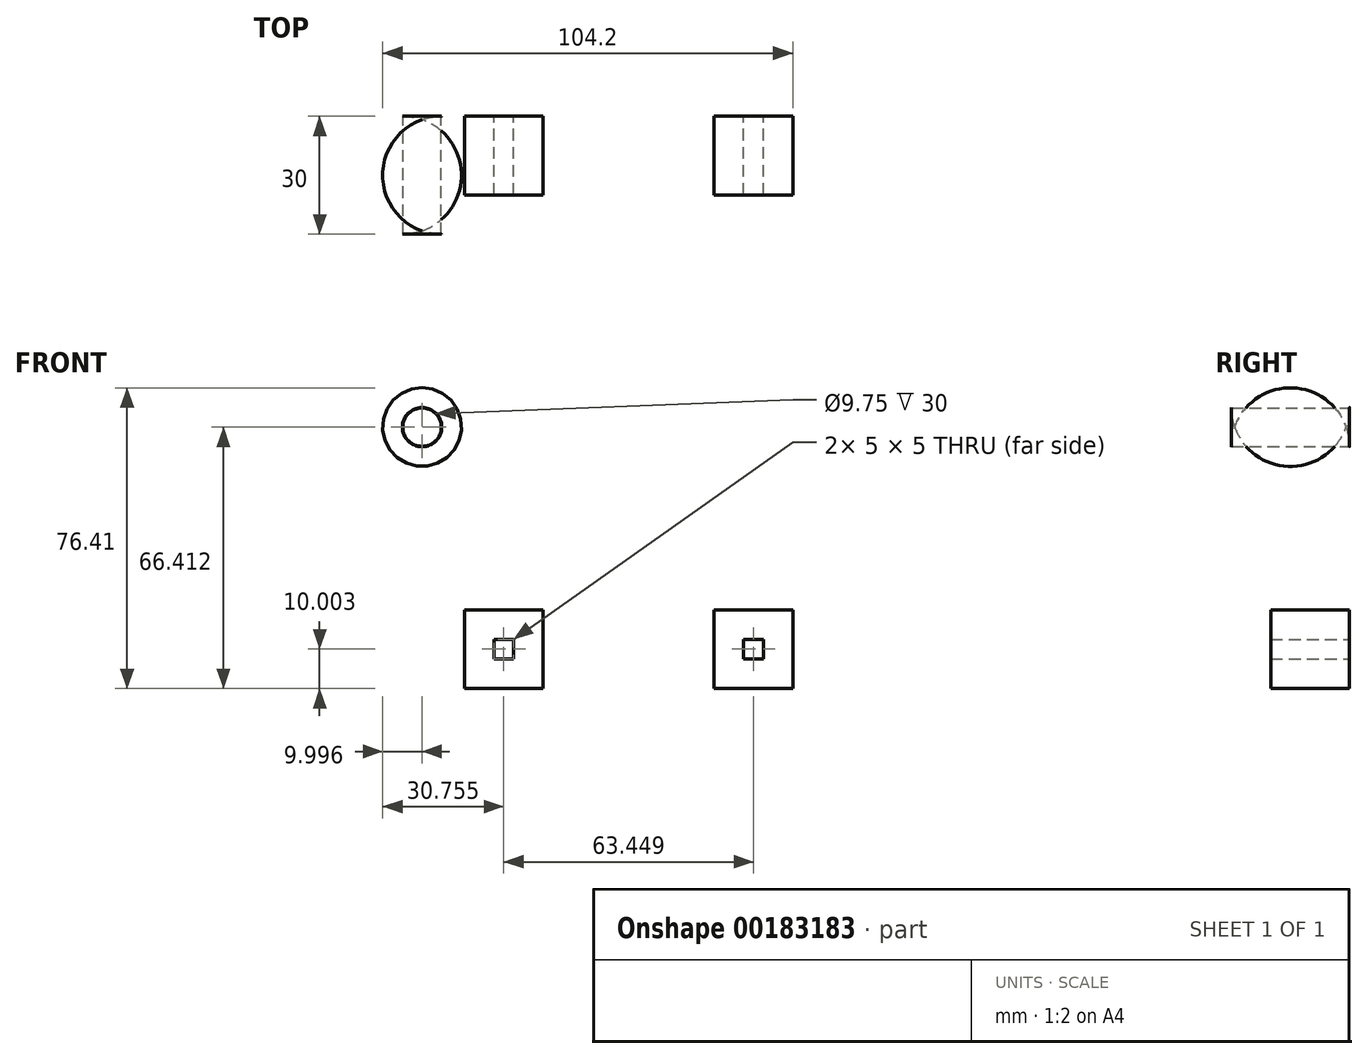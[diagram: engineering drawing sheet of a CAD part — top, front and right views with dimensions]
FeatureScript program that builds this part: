
annotation { "Feature Type Name" : "Feature", "Feature Type Description" : "" }
export const myFeature = defineFeature(function(context is Context, id is Id, definition is map)
    precondition{}
    {
        {
            var Q0;
            Q0=qCreatedBy(makeId("Front.planeOp"),FACE);
            var sketch = newSketch(context, id + "F0", { "sketchPlane" : qUnion([Q0])});
            skCircle(sketch, "E0", {"center": v(-52.48, 29.52) * mm, "radius": 20 * mm});
            skSolve(sketch);
        }
        {
            var Q0;
            Q0 = qSketchRegion(id + "F0", true);
            extrude(context, id + "F1", {"entities" : qUnion([Q0]), "depth" : 30 * mm});
        }
        {
            var Q0;
            Q0=makeQuery(id+"F1.opExtrude","CAP_EDGE",EDGE,{"disambiguationData":[OSD([sQuery(id+"F0.wireOp",EDGE,"E0")])],"isStart":false});
            var Q1;
            Q1=makeQuery(id+"F1.opExtrude","SWEPT_FACE",FACE,{"disambiguationData":[OSD([sQuery(id+"F0.wireOp",EDGE,"E0")])]});
            fillet(context, id + "F2", {"entities" : qUnion([Q0, Q1]), "radius" : 15 * mm, "tangentPropagation" : true, "allowEdgeOverflow" : false});
        }
        {
            var Q0;
            Q0=qCreatedBy(makeId("Front.planeOp"),FACE);
            var sketch = newSketch(context, id + "F3", { "sketchPlane" : qUnion([Q0])});
            skLineSegment(sketch, "E1.bottom", {"start": v(21.72, -16.89) * mm, "end": v(41.72, -16.89) * mm});
            skLineSegment(sketch, "E1.top", {"start": v(21.72, -36.89) * mm, "end": v(41.72, -36.89) * mm});
            skLineSegment(sketch, "E1.left", {"start": v(21.72, -16.89) * mm, "end": v(21.72, -36.89) * mm});
            skLineSegment(sketch, "E1.right", {"start": v(41.72, -16.89) * mm, "end": v(41.72, -36.89) * mm});
            skSolve(sketch);
        }
        {
            var Q0;
            Q0 = qSketchRegion(id + "F3", true);
            extrude(context, id + "F4", {"entities" : qUnion([Q0]), "depth" : 20 * mm});
        }
        {
            var Q0;
            Q0=makeQuery(id+"F4.opExtrude","CAP_FACE",FACE,{"disambiguationData":[OSD([sQuery(id+"F3.wireOp",EDGE,"E1.bottom"),sQuery(id+"F3.wireOp",EDGE,"E1.top"),sQuery(id+"F3.wireOp",EDGE,"E1.left"),sQuery(id+"F3.wireOp",EDGE,"E1.right")])],"isStart":true});
            var sketch = newSketch(context, id + "F5", { "sketchPlane" : qUnion([Q0])});
            skLineSegment(sketch, "E2.bottom", {"start": v(-34.22, -24.39) * mm, "end": v(-29.22, -24.39) * mm});
            skLineSegment(sketch, "E2.top", {"start": v(-34.22, -29.39) * mm, "end": v(-29.22, -29.39) * mm});
            skLineSegment(sketch, "E2.left", {"start": v(-34.22, -24.39) * mm, "end": v(-34.22, -29.39) * mm});
            skLineSegment(sketch, "E2.right", {"start": v(-29.22, -24.39) * mm, "end": v(-29.22, -29.39) * mm});
            skSolve(sketch);
        }
        {
            var Q0;
            Q0=makeQuery(id+"F5.imprint","IMPRINT",FACE,{"disambiguationData":[TD([[makeQuery(id+"F5.imprint","IMPRINT",EDGE,{"derivedFrom":sQuery(id+"F5.wireOp",EDGE,"E2.bottom")}),-1.0]])]});
            extrude(context, id + "F6", {"entities" : qUnion([Q0]), "operationType" : NewBodyOperationType.REMOVE, "oppositeDirection" : true, "depth" : 20 * mm});
        }
        {
            var Q0;
            Q0=makeQuery(id+"F4.opExtrude","SWEPT_BODY",BODY,{"disambiguationData":[OSD([sQuery(id+"F3.wireOp",EDGE,"E1.bottom"),sQuery(id+"F3.wireOp",EDGE,"E1.top"),sQuery(id+"F3.wireOp",EDGE,"E1.left"),sQuery(id+"F3.wireOp",EDGE,"E1.right")])]});
            var Q1;
            Q1=qCreatedBy(makeId("Right.planeOp"),FACE);
            mirror(context, id + "F7", {"entities" : qUnion([Q0]), "mirrorPlane" : qUnion([Q1])});
        }
        {
            var Q0;
            Q0=makeQuery(id+"F1.opExtrude","CAP_FACE",FACE,{"disambiguationData":[OSD([sQuery(id+"F0.wireOp",EDGE,"E0")])],"isStart":true});
            var sketch = newSketch(context, id + "F8", { "sketchPlane" : qUnion([Q0])});
            skCircle(sketch, "E3", {"center": v(52.48, 29.52) * mm, "radius": 4.88 * mm});
            skSolve(sketch);
        }
        {
            var Q0;
            Q0=makeQuery(id+"F8.imprint","IMPRINT",FACE,{"disambiguationData":[TD([[makeQuery(id+"F8.imprint","IMPRINT",EDGE,{"derivedFrom":sQuery(id+"F8.wireOp",EDGE,"E3")}),1.0]])]});
            extrude(context, id + "F9", {"entities" : qUnion([Q0]), "operationType" : NewBodyOperationType.REMOVE, "oppositeDirection" : true, "depth" : 30 * mm});
        }
    });
